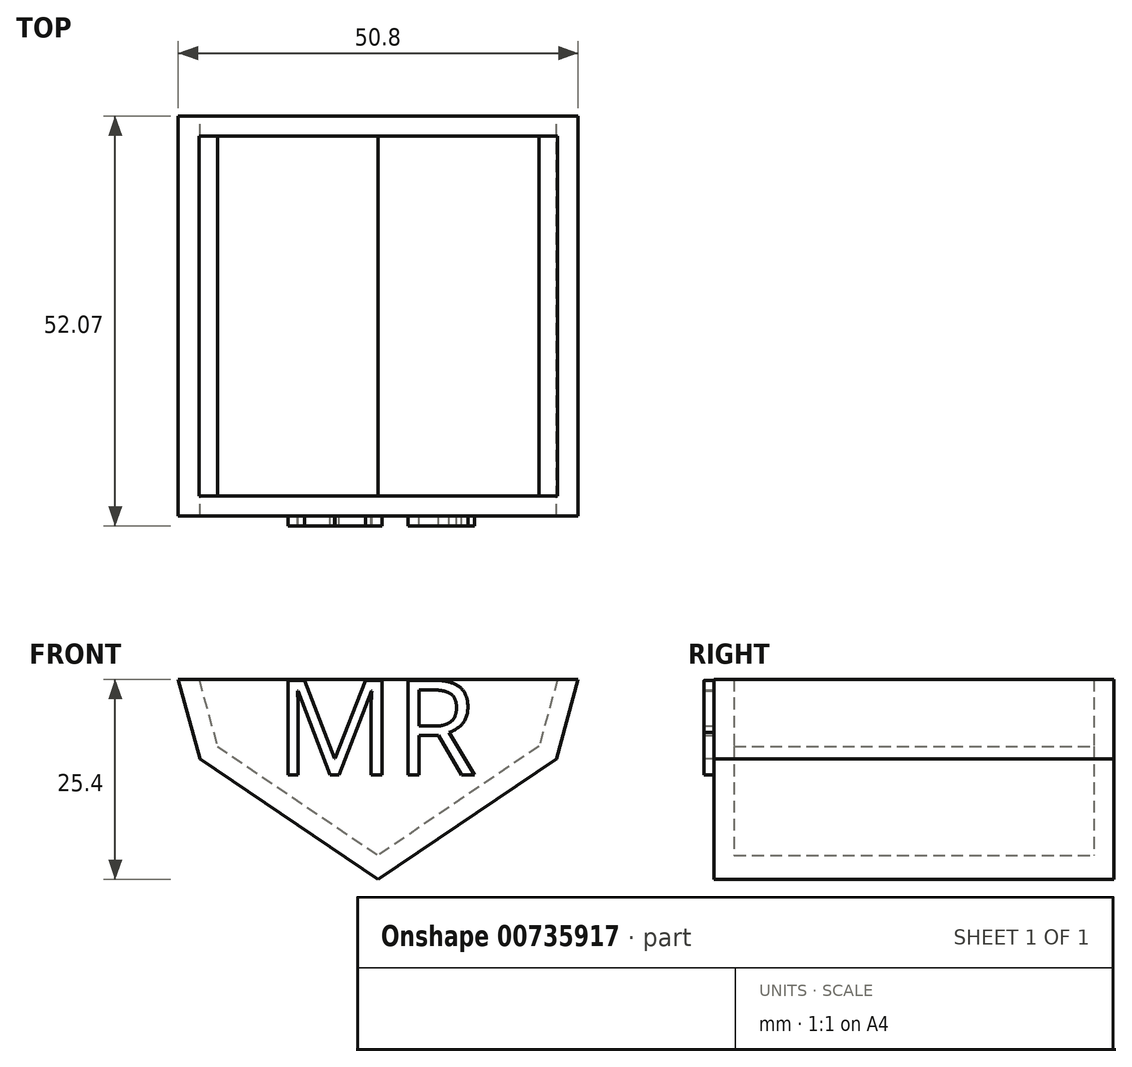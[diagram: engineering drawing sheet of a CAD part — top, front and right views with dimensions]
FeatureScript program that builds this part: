
annotation { "Feature Type Name" : "Feature", "Feature Type Description" : "" }
export const myFeature = defineFeature(function(context is Context, id is Id, definition is map)
    precondition{}
    {
        {
            var Q0;
            Q0=qCreatedBy(makeId("Front.planeOp"),FACE);
            var sketch = newSketch(context, id + "F0", { "sketchPlane" : qUnion([Q0])});
            skLineSegment(sketch, "E0", {"start": v(0, 0) * mm, "end": v(0, -25.4) * mm});
            skLineSegment(sketch, "E1", {"start": v(0, 0) * mm, "end": v(-25.4, 0) * mm});
            skLineSegment(sketch, "E2", {"start": v(-25.4, 0) * mm, "end": v(-22.63, -10.07) * mm});
            skLineSegment(sketch, "E3", {"start": v(-22.63, -10.07) * mm, "end": v(0, -25.4) * mm});
            skLineSegment(sketch, "E4.MirrorCS", {"start": v(25.4, 0) * mm, "end": v(22.63, -10.07) * mm});
            skLineSegment(sketch, "E5.MirrorCS", {"start": v(0, 0) * mm, "end": v(25.4, 0) * mm});
            skLineSegment(sketch, "E6.MirrorCS", {"start": v(22.63, -10.07) * mm, "end": v(0, -25.4) * mm});
            skSolve(sketch);
        }
        {
            var Q0;
            Q0=makeQuery(id+"F0.imprint","IMPRINT",FACE,{"disambiguationData":[TD([[makeQuery(id+"F0.imprint","IMPRINT",EDGE,{"derivedFrom":sQuery(id+"F0.wireOp",EDGE,"E0")}),1.0]])]});
            var Q1;
            Q1=makeQuery(id+"F0.imprint","IMPRINT",FACE,{"disambiguationData":[TD([[makeQuery(id+"F0.imprint","IMPRINT",EDGE,{"derivedFrom":sQuery(id+"F0.wireOp",EDGE,"E0")}),-1.0]])]});
            extrude(context, id + "F1", {"entities" : qUnion([Q0, Q1]), "depth" : 50.8 * mm, "offsetDistance" : 25.4 * mm});
        }
        {
            var Q0;
            Q0=makeQuery(id+"F1.opExtrude","SWEPT_FACE",FACE,{"disambiguationData":[OSD([sQuery(id+"F0.wireOp",EDGE,"E1"),sQuery(id+"F0.wireOp",EDGE,"E5.MirrorCS")])]});
            var sketch = newSketch(context, id + "F2", { "sketchPlane" : qUnion([Q0])});
            skLineSegment(sketch, "E7", {"start": v(0, -50.8) * mm, "end": v(-36.14, -31.84) * mm});
            skLineSegment(sketch, "E8", {"start": v(-36.14, -31.84) * mm, "end": v(-25.4, -109.55) * mm});
            skLineSegment(sketch, "E9", {"start": v(-25.4, -109.55) * mm, "end": v(76.08, -97.56) * mm});
            skLineSegment(sketch, "E10", {"start": v(76.08, -97.56) * mm, "end": v(49.06, -29.59) * mm});
            skLineSegment(sketch, "E11", {"start": v(49.06, -29.59) * mm, "end": v(0, -50.8) * mm});
            skSolve(sketch);
        }
        {
            var Q0;
            {var subQ1=sQuery(id+"F2.wireOp",EDGE,"E8");Q0=makeQuery(id+"F2.imprint","IMPRINT",FACE,{"disambiguationData":[TD([[makeQuery(id+"F2.imprint","IMPRINT",EDGE,{"derivedFrom":subQ1}),1.0]])]});}
            extrude(context, id + "F3", {"entities" : qUnion([Q0]), "operationType" : NewBodyOperationType.REMOVE, "oppositeDirection" : true, "depth" : 59.69 * mm, "offsetDistance" : 25.4 * mm});
        }
        {
            var Q0;
            Q0=makeQuery(id+"F1.opExtrude","SWEPT_FACE",FACE,{"disambiguationData":[OSD([sQuery(id+"F0.wireOp",EDGE,"E1"),sQuery(id+"F0.wireOp",EDGE,"E5.MirrorCS")])]});
            var Q1;
            Q1=makeQuery(id+"F1.opExtrude","SWEPT_BODY",BODY,{"disambiguationData":[OSD([sQuery(id+"F0.wireOp",EDGE,"E1"),sQuery(id+"F0.wireOp",EDGE,"E2"),sQuery(id+"F0.wireOp",EDGE,"E3"),sQuery(id+"F0.wireOp",EDGE,"E4.MirrorCS"),sQuery(id+"F0.wireOp",EDGE,"E5.MirrorCS"),sQuery(id+"F0.wireOp",EDGE,"E6.MirrorCS")])]});
            shell(context, id + "F4", {"entities" : qUnion([Q0]), "parts" : qUnion([Q1]), "thickness" : 76.2 * mm});
        }
        {
            var Q0;
            Q0=makeQuery(id+"F1.opExtrude","SWEPT_FACE",FACE,{"disambiguationData":[OSD([sQuery(id+"F0.wireOp",EDGE,"E1"),sQuery(id+"F0.wireOp",EDGE,"E5.MirrorCS")])]});
            shell(context, id + "F5", {"entities" : qUnion([Q0]), "thickness" : 2.54 * mm});
        }
        {
            var Q0;
            Q0=makeQuery(id+"F1.opExtrude","CAP_FACE",FACE,{"disambiguationData":[OSD([sQuery(id+"F0.wireOp",EDGE,"E1"),sQuery(id+"F0.wireOp",EDGE,"E2"),sQuery(id+"F0.wireOp",EDGE,"E3"),sQuery(id+"F0.wireOp",EDGE,"E4.MirrorCS"),sQuery(id+"F0.wireOp",EDGE,"E5.MirrorCS"),sQuery(id+"F0.wireOp",EDGE,"E6.MirrorCS")])],"isStart":false});
            var sketch = newSketch(context, id + "F6", { "sketchPlane" : qUnion([Q0])});
            skText(sketch, "E12", { "text": "MR", "fontName": "OpenSans-Regular.ttf"});
            const initialGuessF6  = {"E12": [-0.01309, -0.01213, 1, 0, 0.01213]};
            skSetInitialGuess(sketch, initialGuessF6);
            skSolve(sketch);
        }
        {
            var Q0;
            Q0 = qSketchRegion(id + "F6", true);
            extrude(context, id + "F7", {"entities" : qUnion([Q0]), "operationType" : NewBodyOperationType.ADD, "depth" : 1.27 * mm, "offsetDistance" : 25.4 * mm});
        }
    });
